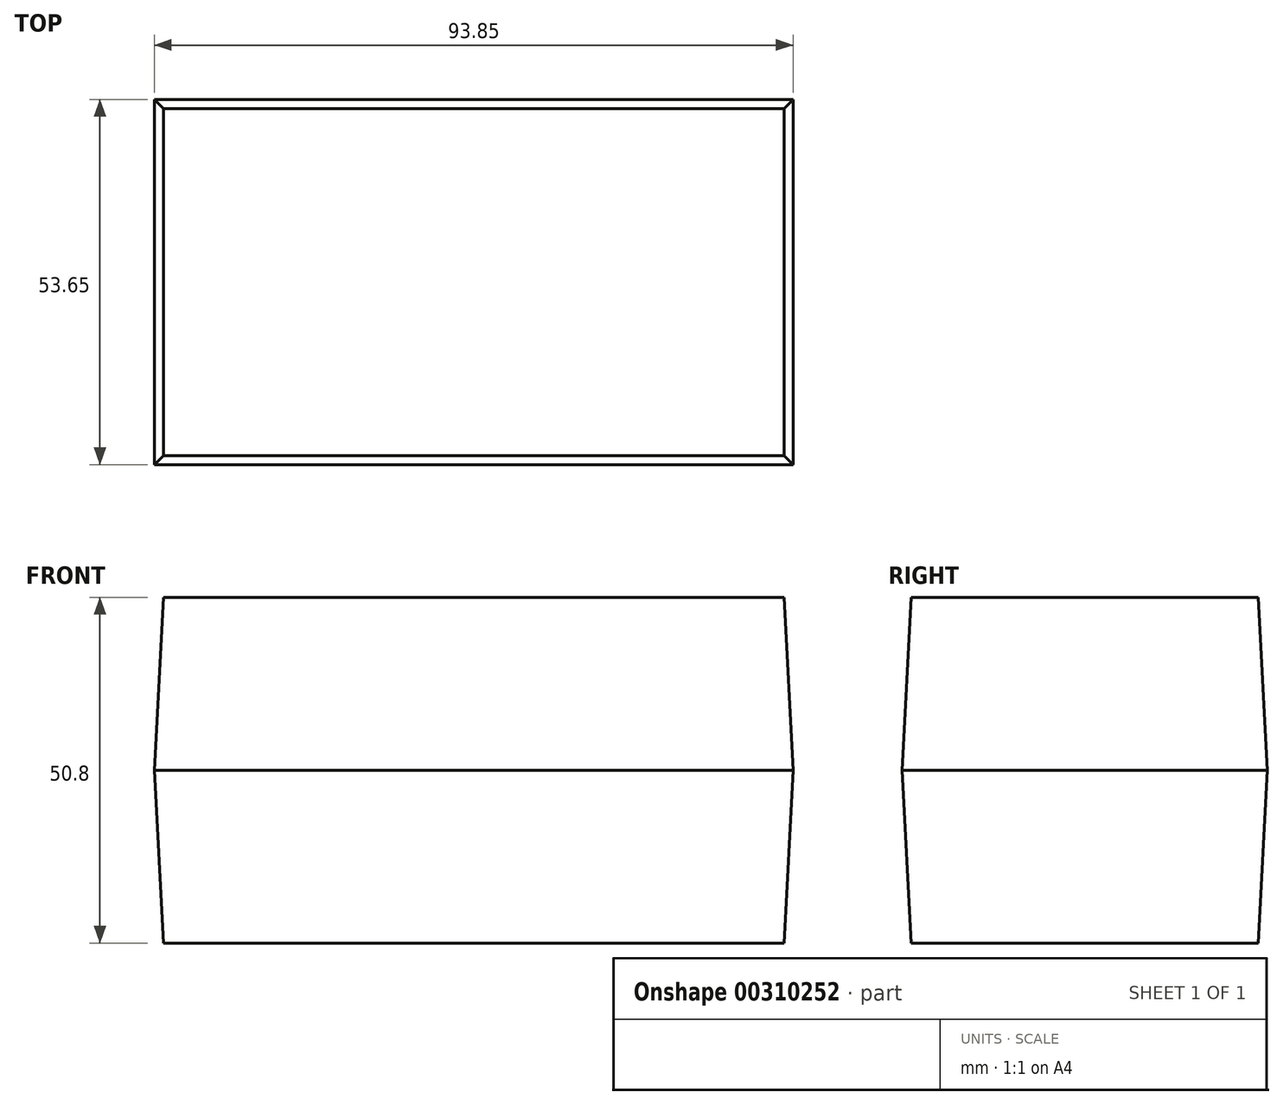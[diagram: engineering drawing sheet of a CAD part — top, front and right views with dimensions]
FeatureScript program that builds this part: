
annotation { "Feature Type Name" : "Feature", "Feature Type Description" : "" }
export const myFeature = defineFeature(function(context is Context, id is Id, definition is map)
    precondition{}
    {
        {
            var Q0;
            Q0=qCreatedBy(makeId("Top.planeOp"),FACE);
            var sketch = newSketch(context, id + "F0", { "sketchPlane" : qUnion([Q0])});
            skLineSegment(sketch, "E0.bottom", {"start": v(-44.93, 26.73) * mm, "end": v(48.92, 26.73) * mm});
            skLineSegment(sketch, "E0.top", {"start": v(-44.93, -26.92) * mm, "end": v(48.92, -26.92) * mm});
            skLineSegment(sketch, "E0.left", {"start": v(-44.93, 26.73) * mm, "end": v(-44.93, -26.92) * mm});
            skLineSegment(sketch, "E0.right", {"start": v(48.92, 26.73) * mm, "end": v(48.92, -26.92) * mm});
            skSolve(sketch);
        }
        {
            var Q0;
            Q0 = qSketchRegion(id + "F0", true);
            extrude(context, id + "F1", {"entities" : qUnion([Q0]), "depth" : 25.4 * mm, "hasDraft" : true, "draftAngle" : 3 * degree, "draftPullDirection" : true, "hasSecondDirection" : true, "secondDirectionOppositeDirection" : true, "secondDirectionDepth" : 25.4 * mm, "hasSecondDirectionDraft" : true, "secondDirectionDraftAngle" : 3 * degree, "secondDirectionDraftPullDirection" : true});
        }
    });
